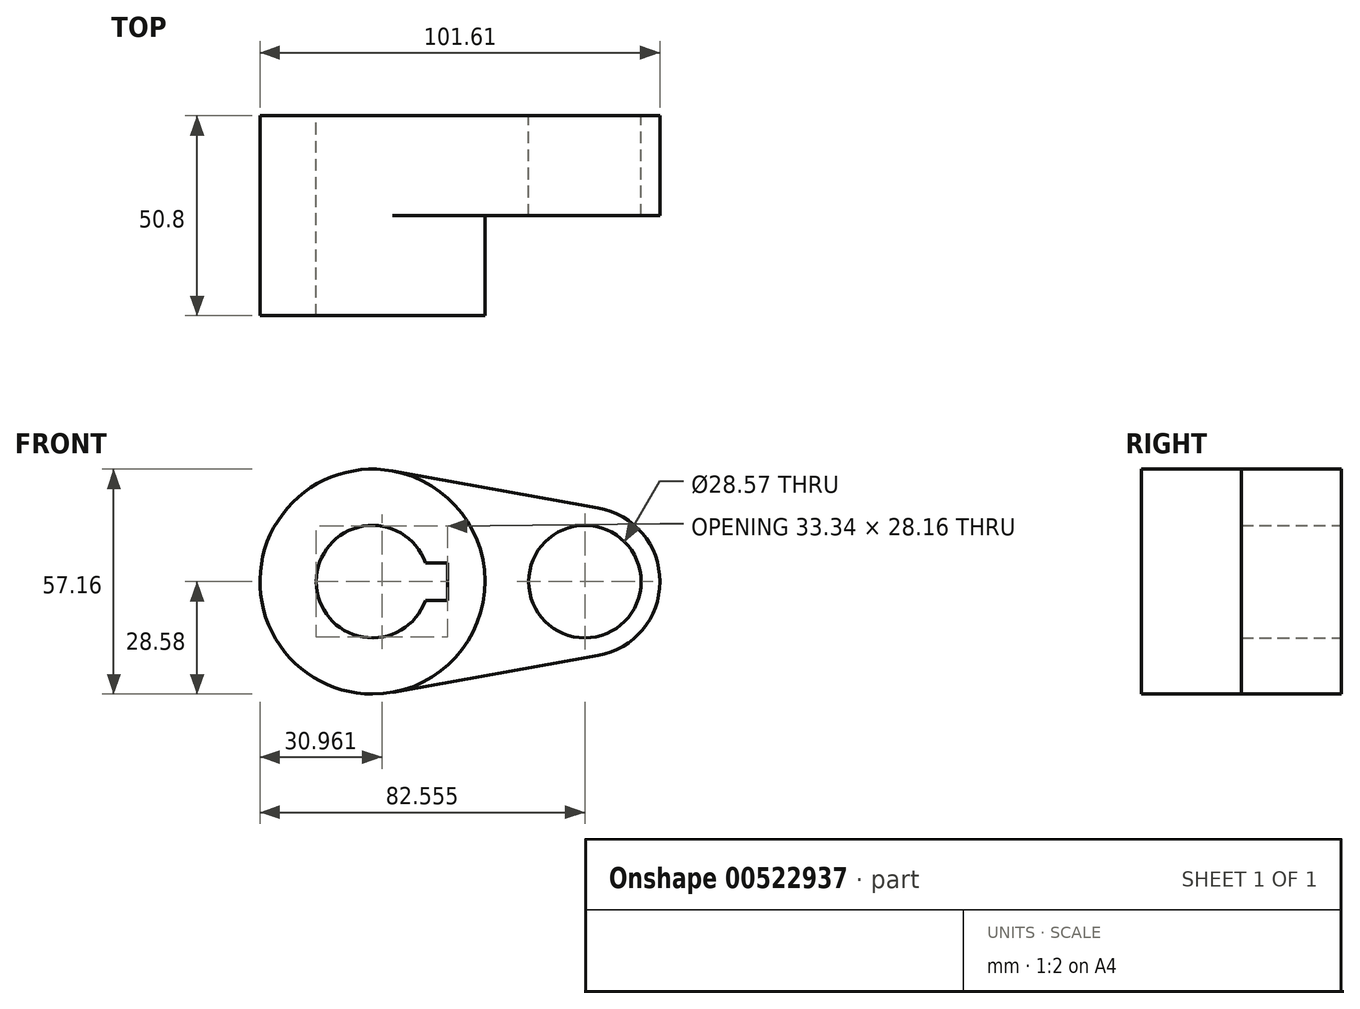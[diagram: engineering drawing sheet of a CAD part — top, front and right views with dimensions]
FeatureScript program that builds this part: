
annotation { "Feature Type Name" : "Feature", "Feature Type Description" : "" }
export const myFeature = defineFeature(function(context is Context, id is Id, definition is map)
    precondition{}
    {
        {
            var Q0;
            Q0=qCreatedBy(makeId("Front.planeOp"),FACE);
            var sketch = newSketch(context, id + "F0", { "sketchPlane" : qUnion([Q0])});
            skCircle(sketch, "E0", {"center": v(0, 0) * mm, "radius": 28.58 * mm});
            skCircle(sketch, "E1", {"center": v(53.98, 0) * mm, "radius": 19.05 * mm});
            skLineSegment(sketch, "E2", {"start": v(5.04, 28.13) * mm, "end": v(57.34, 18.75) * mm});
            skLineSegment(sketch, "E3", {"start": v(5.04, -28.13) * mm, "end": v(57.34, -18.75) * mm});
            skCircle(sketch, "E4", {"center": v(0, 0) * mm, "radius": 14.29 * mm});
            skCircle(sketch, "E5", {"center": v(53.98, 0) * mm, "radius": 14.29 * mm});
            skLineSegment(sketch, "E6.bottom", {"start": v(-19.05, 4.76) * mm, "end": v(19.05, 4.76) * mm});
            skLineSegment(sketch, "E6.top", {"start": v(-19.05, -4.76) * mm, "end": v(19.05, -4.76) * mm});
            skLineSegment(sketch, "E6.left", {"start": v(-19.05, 4.76) * mm, "end": v(-19.05, -4.76) * mm});
            skLineSegment(sketch, "E6.right", {"start": v(19.05, 4.76) * mm, "end": v(19.05, -4.76) * mm});
            skSolve(sketch);
        }
        {
            var Q0;
            {var subQ7=sQuery(id+"F0.wireOp",EDGE,"E6.left");Q0=makeQuery(id+"F0.imprint","IMPRINT",FACE,{"disambiguationData":[TD([[makeQuery(id+"F0.imprint","IMPRINT",EDGE,{"derivedFrom":subQ7}),-1.0]])]});}
            var Q1;
            {var subQ5=sQuery(id+"F0.wireOp",EDGE,"E6.left");Q1=makeQuery(id+"F0.imprint","IMPRINT",FACE,{"disambiguationData":[TD([[makeQuery(id+"F0.imprint","IMPRINT",EDGE,{"derivedFrom":subQ5}),1.0]])]});}
            var Q2;
            {var subQ0=sQuery(id+"F0.wireOp",EDGE,"E2");Q2=makeQuery(id+"F0.imprint","IMPRINT",FACE,{"disambiguationData":[TD([[makeQuery(id+"F0.imprint","IMPRINT",EDGE,{"derivedFrom":subQ0}),-1.0]])]});}
            var Q3;
            Q3=makeQuery(id+"F0.imprint","IMPRINT",FACE,{"disambiguationData":[TD([[makeQuery(id+"F0.imprint","IMPRINT",EDGE,{"derivedFrom":sQuery(id+"F0.wireOp",EDGE,"E5")}),-1.0]])]});
            extrude(context, id + "F1", {"entities" : qUnion([Q0, Q1, Q2, Q3]), "depth" : 25.4 * mm, "offsetDistance" : 25.4 * mm});
        }
        {
            var Q0;
            {var subQ7=sQuery(id+"F0.wireOp",EDGE,"E6.left");Q0=makeQuery(id+"F0.imprint","IMPRINT",FACE,{"disambiguationData":[TD([[makeQuery(id+"F0.imprint","IMPRINT",EDGE,{"derivedFrom":subQ7}),-1.0]])]});}
            var Q1;
            {var subQ5=sQuery(id+"F0.wireOp",EDGE,"E6.left");Q1=makeQuery(id+"F0.imprint","IMPRINT",FACE,{"disambiguationData":[TD([[makeQuery(id+"F0.imprint","IMPRINT",EDGE,{"derivedFrom":subQ5}),1.0]])]});}
            extrude(context, id + "F2", {"entities" : qUnion([Q0, Q1]), "operationType" : NewBodyOperationType.ADD, "depth" : 50.8 * mm, "offsetDistance" : 25.4 * mm});
        }
    });
